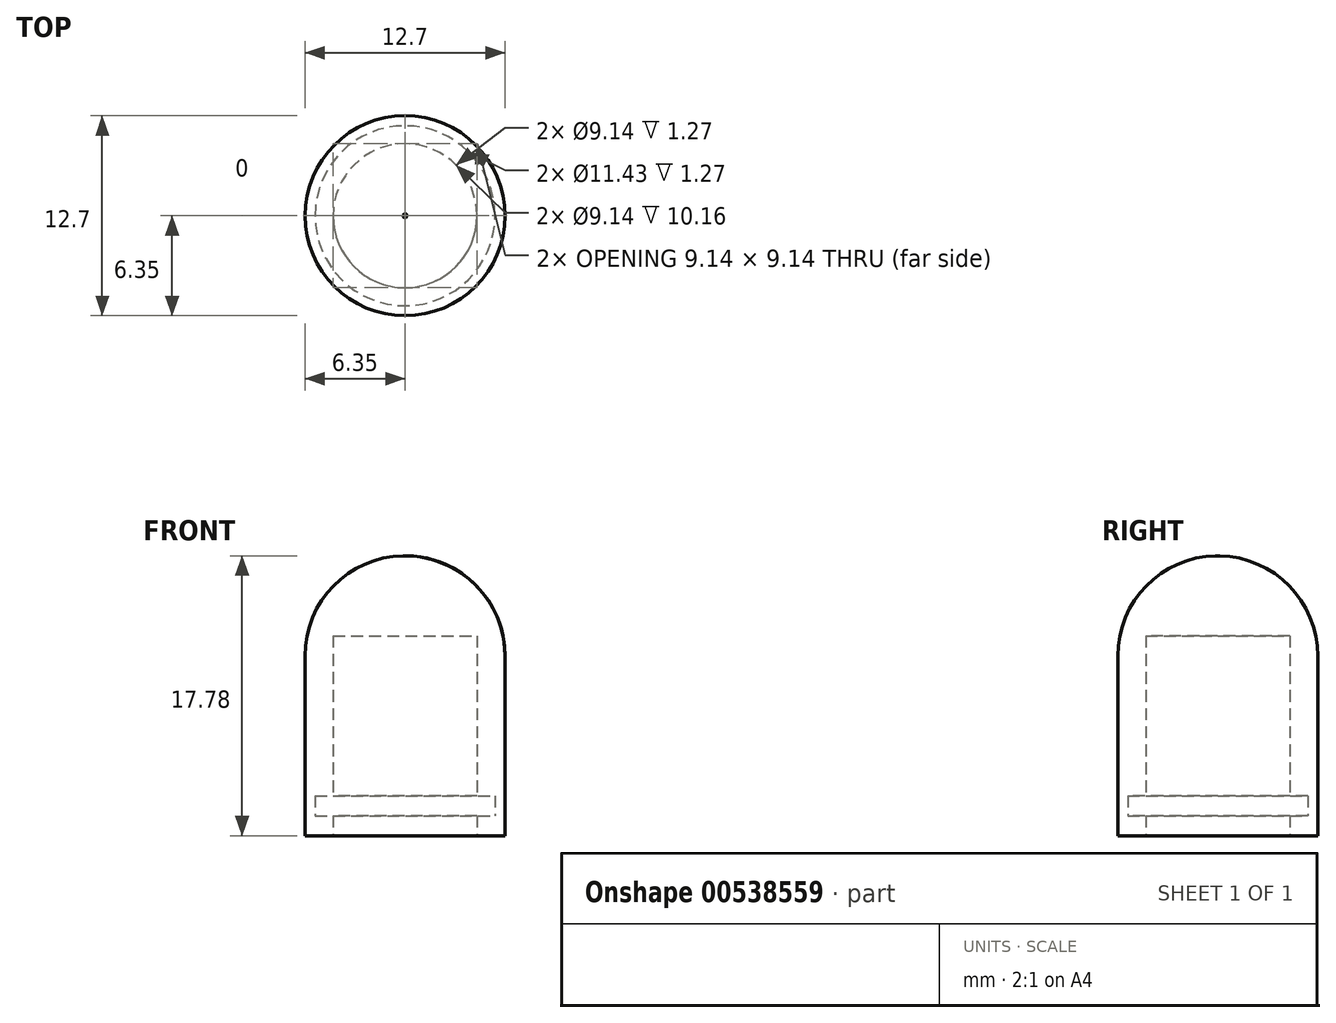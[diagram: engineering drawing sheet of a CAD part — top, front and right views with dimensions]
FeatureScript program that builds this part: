
annotation { "Feature Type Name" : "Feature", "Feature Type Description" : "" }
export const myFeature = defineFeature(function(context is Context, id is Id, definition is map)
    precondition{}
    {
        {
            var Q0;
            Q0=qCreatedBy(makeId("Top.planeOp"),FACE);
            var sketch = newSketch(context, id + "F0", { "sketchPlane" : qUnion([Q0])});
            skCircle(sketch, "E0", {"center": v(0, 0) * mm, "radius": 6.35 * mm});
            skSolve(sketch);
        }
        {
            var Q0;
            Q0=makeQuery(id+"F0.imprint","IMPRINT",FACE,{"disambiguationData":[TD([[makeQuery(id+"F0.imprint","IMPRINT",EDGE,{"derivedFrom":sQuery(id+"F0.wireOp",EDGE,"E0")}),1.0]])]});
            extrude(context, id + "F1", {"entities" : qUnion([Q0]), "depth" : 17.78 * mm, "offsetDistance" : 25.4 * mm});
        }
        {
            var Q0;
            Q0=qCreatedBy(makeId("Front.planeOp"),FACE);
            var sketch = newSketch(context, id + "F2", { "sketchPlane" : qUnion([Q0])});
            skArc(sketch, "E1", {"start": v(-0.13, 17.78) * mm, "mid": v(-4.53, 15.88) * mm, "end": v(-6.35, 11.43) * mm});
            skLineSegment(sketch, "E2", {"start": v(-0.13, 17.78) * mm, "end": v(-6.35, 17.78) * mm});
            skLineSegment(sketch, "E3", {"start": v(-6.35, 17.78) * mm, "end": v(-6.35, 11.43) * mm});
            skLineSegment(sketch, "E4", {"start": v(0, 0) * mm, "end": v(-6.35, 0) * mm, "construction": true});
            skSolve(sketch);
        }
        {
            var Q0;
            Q0=qCreatedBy(makeId("Front.planeOp"),FACE);
            var sketch = newSketch(context, id + "F3", { "sketchPlane" : qUnion([Q0])});
            skLineSegment(sketch, "E5", {"start": v(0, 0) * mm, "end": v(0, 25.4) * mm, "construction": true});
            skSolve(sketch);
        }
        {
            var Q0;
            Q0 = qSketchRegion(id + "F2", true);
            var Q1;
            Q1=sQuery(id+"F3.wireOp",EDGE,"E5");
            revolve(context, id + "F4", {"operationType" : NewBodyOperationType.REMOVE, "entities" : qUnion([Q0]), "axis" : qUnion([Q1]), "revolveType" : RevolveType.FULL, "oppositeDirection" : true});
        }
        {
            var Q0;
            Q0=makeQuery(id+"F1.opExtrude","CAP_FACE",FACE,{"disambiguationData":[OSD([sQuery(id+"F0.wireOp",EDGE,"E0")])],"isStart":true});
            var sketch = newSketch(context, id + "F5", { "sketchPlane" : qUnion([Q0])});
            skCircle(sketch, "E6", {"center": v(0, 0) * mm, "radius": 4.57 * mm});
            skSolve(sketch);
        }
        {
            var Q0;
            Q0=makeQuery(id+"F5.imprint","IMPRINT",FACE,{"disambiguationData":[TD([[makeQuery(id+"F5.imprint","IMPRINT",EDGE,{"derivedFrom":sQuery(id+"F5.wireOp",EDGE,"E6")}),1.0]])]});
            extrude(context, id + "F6", {"entities" : qUnion([Q0]), "operationType" : NewBodyOperationType.REMOVE, "oppositeDirection" : true, "depth" : 12.7 * mm, "offsetDistance" : 25.4 * mm});
        }
        {
            var Q0;
            Q0=qCreatedBy(makeId("Right.planeOp"),FACE);
            var sketch = newSketch(context, id + "F7", { "sketchPlane" : qUnion([Q0])});
            skLineSegment(sketch, "E7", {"start": v(0, 0) * mm, "end": v(0, 65.08) * mm, "construction": true});
            skLineSegment(sketch, "E8.bottom", {"start": v(-5.72, 1.27) * mm, "end": v(0, 1.27) * mm});
            skLineSegment(sketch, "E8.top", {"start": v(-5.72, 2.54) * mm, "end": v(0, 2.54) * mm});
            skLineSegment(sketch, "E8.left", {"start": v(-5.72, 1.27) * mm, "end": v(-5.72, 2.54) * mm});
            skLineSegment(sketch, "E8.right", {"start": v(0, 1.27) * mm, "end": v(0, 2.54) * mm});
            skSolve(sketch);
        }
        {
            var Q0;
            Q0 = qSketchRegion(id + "F7", true);
            var Q1;
            Q1=sQuery(id+"F7.wireOp",EDGE,"E8.right");
            revolve(context, id + "F8", {"operationType" : NewBodyOperationType.REMOVE, "entities" : qUnion([Q0]), "axis" : qUnion([Q1]), "revolveType" : RevolveType.FULL});
        }
    });
